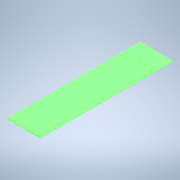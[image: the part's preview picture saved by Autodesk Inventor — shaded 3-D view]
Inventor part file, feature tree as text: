
AUTODESK INVENTOR PART (.ipt)
format: ipt  version: 2022 (Build 260153000, 153)  size: 140,288 bytes
history: native  units: mm
features: sketch x3, hole x2, other x1, extrude x1, chamfer x1
ambient origin geometry x8: Origin, YZ Plane, XZ Plane, XY Plane, X Axis, Y Axis, Z Axis, Center Point
bodies: Body1 (feature_tree)
feature tree (8):
  other  "ソリッド1"
  extrude  "押し出し1"  Depth=319.5mm
  hole  "穴1"  [1 undecoded]
  chamfer  "面取り2"  Distance=2.0mm
  hole  "穴2"  [1 undecoded]
  sketch  "スケッチ1"
  sketch  "スケッチ3"
  sketch  "スケッチ5"
note: 2 required parameter values undecoded (feature->parameter linkage not recoverable at this tier; creation-order binding heuristic only, values carry confidence <= 0.55)
